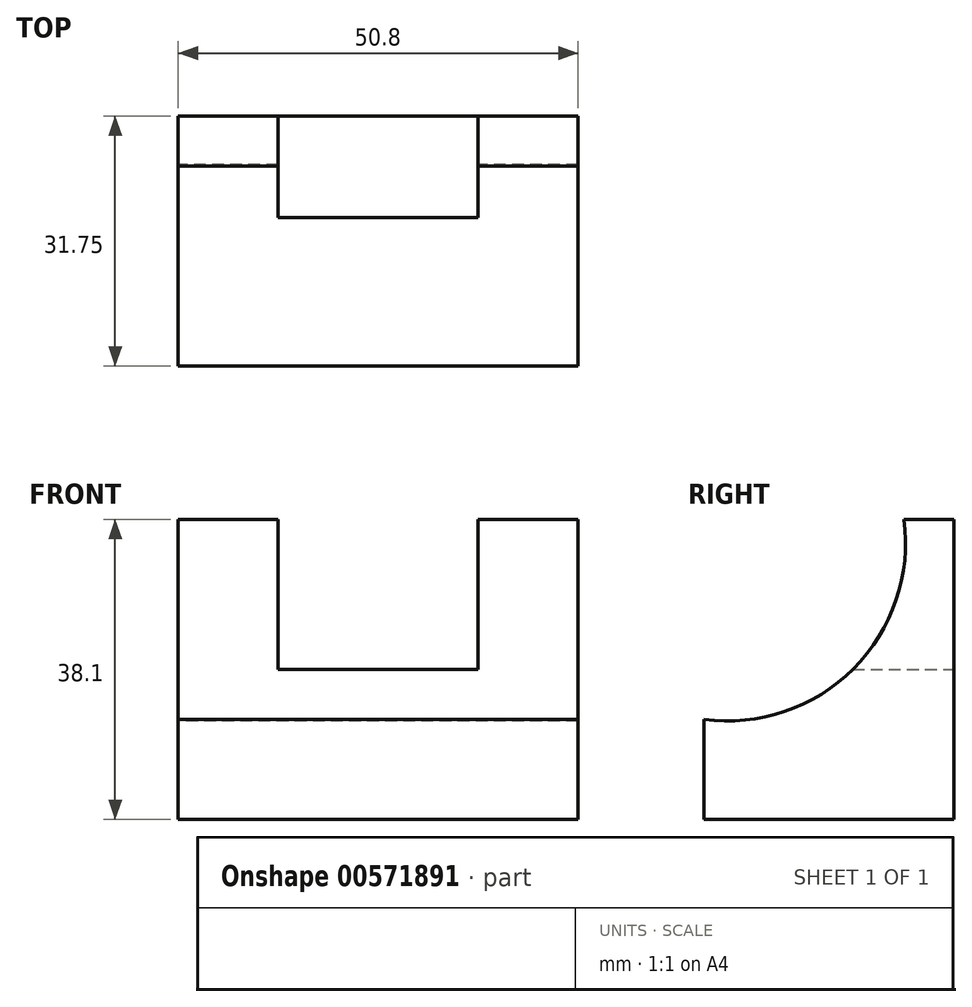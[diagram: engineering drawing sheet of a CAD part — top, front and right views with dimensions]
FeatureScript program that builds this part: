
annotation { "Feature Type Name" : "Feature", "Feature Type Description" : "" }
export const myFeature = defineFeature(function(context is Context, id is Id, definition is map)
    precondition{}
    {
        {
            var Q0;
            Q0=qCreatedBy(makeId("Right.planeOp"),FACE);
            var sketch = newSketch(context, id + "F0", { "sketchPlane" : qUnion([Q0])});
            skLineSegment(sketch, "E0", {"start": v(-23.87, 0) * mm, "end": v(7.88, 0) * mm});
            skLineSegment(sketch, "E1", {"start": v(7.88, 0) * mm, "end": v(7.88, 38.1) * mm});
            skLineSegment(sketch, "E2", {"start": v(-23.87, 0) * mm, "end": v(-23.87, 38.1) * mm});
            skLineSegment(sketch, "E3", {"start": v(-23.87, 38.1) * mm, "end": v(7.88, 38.1) * mm});
            skSolve(sketch);
        }
        {
            var Q0;
            Q0=makeQuery(id+"F0.imprint","IMPRINT",FACE,{"disambiguationData":[TD([[makeQuery(id+"F0.imprint","IMPRINT",EDGE,{"derivedFrom":sQuery(id+"F0.wireOp",EDGE,"E0")}),1.0]])]});
            extrude(context, id + "F1", {"entities" : qUnion([Q0]), "depth" : 50.8 * mm, "offsetDistance" : 25.4 * mm});
        }
        {
            var Q0;
            Q0=makeQuery(id+"F1.opExtrude","CAP_FACE",FACE,{"disambiguationData":[OSD([sQuery(id+"F0.wireOp",EDGE,"E0"),sQuery(id+"F0.wireOp",EDGE,"E1"),sQuery(id+"F0.wireOp",EDGE,"E2"),sQuery(id+"F0.wireOp",EDGE,"E3")])],"isStart":true});
            var sketch = newSketch(context, id + "F2", { "sketchPlane" : qUnion([Q0])});
            skArc(sketch, "E4", {"start": v(-1.53, 38.1) * mm, "mid": v(4.9, 19.14) * mm, "end": v(23.87, 12.7) * mm});
            skSolve(sketch);
        }
        {
            var Q0;
            {var subQ0=sQuery(id+"F2.wireOp",EDGE,"E4");Q0=makeQuery(id+"F2.imprint","IMPRINT",FACE,{"disambiguationData":[TD([[makeQuery(id+"F2.imprint","IMPRINT",EDGE,{"derivedFrom":subQ0}),1.0]])]});}
            extrude(context, id + "F3", {"entities" : qUnion([Q0]), "operationType" : NewBodyOperationType.REMOVE, "endBound" : BoundingType.THROUGH_ALL, "oppositeDirection" : true, "depth" : 25.4 * mm, "offsetDistance" : 25.4 * mm});
        }
        {
            var Q0;
            Q0=makeQuery(id+"F1.opExtrude","SWEPT_FACE",FACE,{"disambiguationData":[OSD([sQuery(id+"F0.wireOp",EDGE,"E1")])]});
            var sketch = newSketch(context, id + "F4", { "sketchPlane" : qUnion([Q0])});
            skLineSegment(sketch, "E5", {"start": v(-38.1, 38.1) * mm, "end": v(-38.1, 19.05) * mm});
            skLineSegment(sketch, "E6", {"start": v(-38.1, 19.05) * mm, "end": v(-12.7, 19.05) * mm});
            skLineSegment(sketch, "E7", {"start": v(-12.7, 19.05) * mm, "end": v(-12.7, 38.1) * mm});
            skSolve(sketch);
        }
        {
            var Q0;
            {var subQ0=sQuery(id+"F4.wireOp",EDGE,"E5");Q0=makeQuery(id+"F4.imprint","IMPRINT",FACE,{"disambiguationData":[TD([[makeQuery(id+"F4.imprint","IMPRINT",EDGE,{"derivedFrom":subQ0}),1.0]])]});}
            extrude(context, id + "F5", {"entities" : qUnion([Q0]), "operationType" : NewBodyOperationType.REMOVE, "endBound" : BoundingType.THROUGH_ALL, "oppositeDirection" : true, "depth" : 25.4 * mm, "offsetDistance" : 25.4 * mm});
        }
    });
